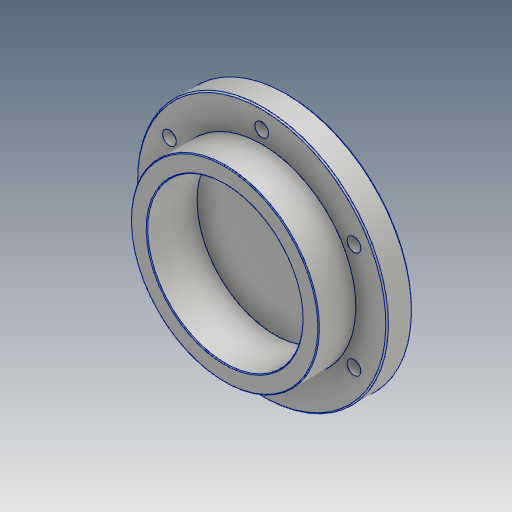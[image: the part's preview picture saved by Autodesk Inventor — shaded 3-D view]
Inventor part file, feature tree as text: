
AUTODESK INVENTOR PART (.ipt)
format: ipt  version: 2018.2 (Build 222227000, 227)  size: 227,840 bytes
history: native  units: mm
features: sketch x3, other x2, chamfer x2, hole x1
ambient origin geometry x8: Origin, YZ Plane, XZ Plane, XY Plane, X Axis, Y Axis, Z Axis, Center Point
bodies: Body1 (feature_tree)
feature tree (8):
  other  "200-10-ROCKER-BEARING-01.ipt"
  other  "Grundkoerper"
  hole  "DIN7984_M5"  [1 undecoded]
  chamfer  "Fase_Passung"  Distance=0.3mm Angle=45.0deg
  chamfer  "Fase_Allgemein"  Distance=0.5mm Angle=45.0deg
  sketch  "Skizze_Lagersitz"  dims[d60=60.0mm d62=360.0deg d64=5.5mm d65=6.0mm d66=10.0mm d67=3.9mm d68=90.0deg d69=8.0mm d70=20.594885mm d74=5.0mm d79=30.2mm d81=25.0mm]
  sketch  "Skizze4"  dims[d32=10.0mm d35=90.0deg d50=0.3mm d51=2.0mm d52=45.0deg d53=0.5mm d54=2.0mm d55=45.0deg]
  sketch  "Skizze6"  dims[d59=85.0mm]
note: 1 required parameter value undecoded (feature->parameter linkage not recoverable at this tier; creation-order binding heuristic only, values carry confidence <= 0.55)
